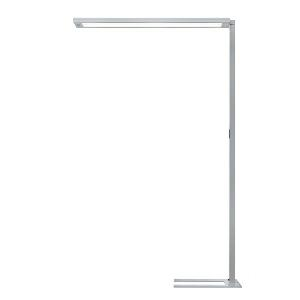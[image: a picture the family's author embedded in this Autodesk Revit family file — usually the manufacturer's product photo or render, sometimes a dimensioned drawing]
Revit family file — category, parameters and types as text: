
# Revit family: lavigo_-_dps_16000_840_r_g2_00802640_0bb4
name_source: partatom
category: Lighting Fixtures
units: mm (PartAtom-declared; Revit-internal decimal feet)

## family parameters
Cut with Voids When Loaded = No
Host = Face
Light Source = No
Part Type = Normal
Room Calculation Point = No
Round Connector Dimension = Use Diameter
Shared = No

## types (1)
- LAVIGO - DPS 16000/840/R/G2 (1 x LED, 16450 lm, 4000K)
    Apparent Load = 112 VA
    Approval mark = CE
    CIE Flux Codes = 60 87 97 11 100
    Color Rendering = 80-89
    Color Temperature = 4000K
    Control Gear = Electronic ballast
    Default Elevation = 1800 mm
    Description = DPS 16000/840/R/G2|Free-standing luminaire|light source: LED|work equipment: Electronic ballast DALI|connected load: 220-240 V, 50/60 Hz|Power consumption: approx. 112 W|standby: approx. 0,50|power factor: approx. 0,940|luminous flux: 16450 lm|luminous efficacy: 146 lm/W|light distribution: Direct/indirect|direct ratio: approx. 11 %|colour temperature: Cold white, ca. 4000 K|color rendering index (CRI): >= 80|chromaticity tolerance:  3 SDCM|technology: Presence and daylight sensor control (PIR)|operation: Multi-function switch|luminaire body|material: Steel/plastic|surface: Powder coatet|colour: Silver metallic|lamp cover: Polycarbonate (PC), Clear, Structured|tubular section|material: Steel tube|surface: Powder-coated|Form: Tubular section upright|colour of tubular section: Silver metallic|luminaire base|Form: C-form flat|weight (net): approx. 21.4 kg|mains lead: 3.00 m Mains plug CEE 7/VII|Fastening: Floor standing base|decorative contrast side parts: Flint grey|glare control: Prism aperture|luminance(L65): <= 2800 cd/m|unified glare rating(4H 8H): <=  16|special features: Luminaire head detachable, Cradle to Cradle Certified TM, Direct light component with edge light and light-guide technology for homogenous light exit, Flicker-free, Integrated light and presence sensor PIR, Retrofittable with TALK module, Separated, direct and indirect light individually adjustable|Approval mark: VDE - ENEC|
    Frequency = 50 Hz
    Height = 36 mm
    Lamp = 1 x LED
    Lamp Light Flux = 16450 lm
    Lamp count = 1
    Length = 1265 mm
    Luminous efficacy = 147 lm/W
    Manufacturer = Waldmann
    ModVariant = No
    Model = 00802640
    Mounting Place = Floor
    Mounting Type = Freestanding
    Number of Poles = 1
    OnlyDefault = Yes
    Power Factor = 1
    Product Name = LAVIGO - DPS 16000/840/R/G2
    Product group = Free standing luminaire
    ProductGroupID = 13
    Protection Class = Protection class I
    Protection Degree = IP 20
    RLX_Detail_Level = 1
    RLX_Emergency_Light_Flux = 0 lm
    RLX_Emergency_Type = 0
    RLX_Emergency_Type_DB = No
    RlxData = <blob elided: 31905 chars, md5=dfedfc79>
    Socket = socket
    Standby Power = 0 W
    System Light Flux = 16450 lm
    System Power = 112 W
    Type Comments = Product without accessories
    Type Image = 121763000-00710211.jpg
    URL = http://relux.com
    VarID = ---
    Voltage = 230 V
    Voltage Range = 220-240 V
    Weight = 0.00 kg
    Width = 201 mm

## geometry (parser evidence)
native form markers: Blend x4, Sweep x14
no freeform markers — native parametric forms only
